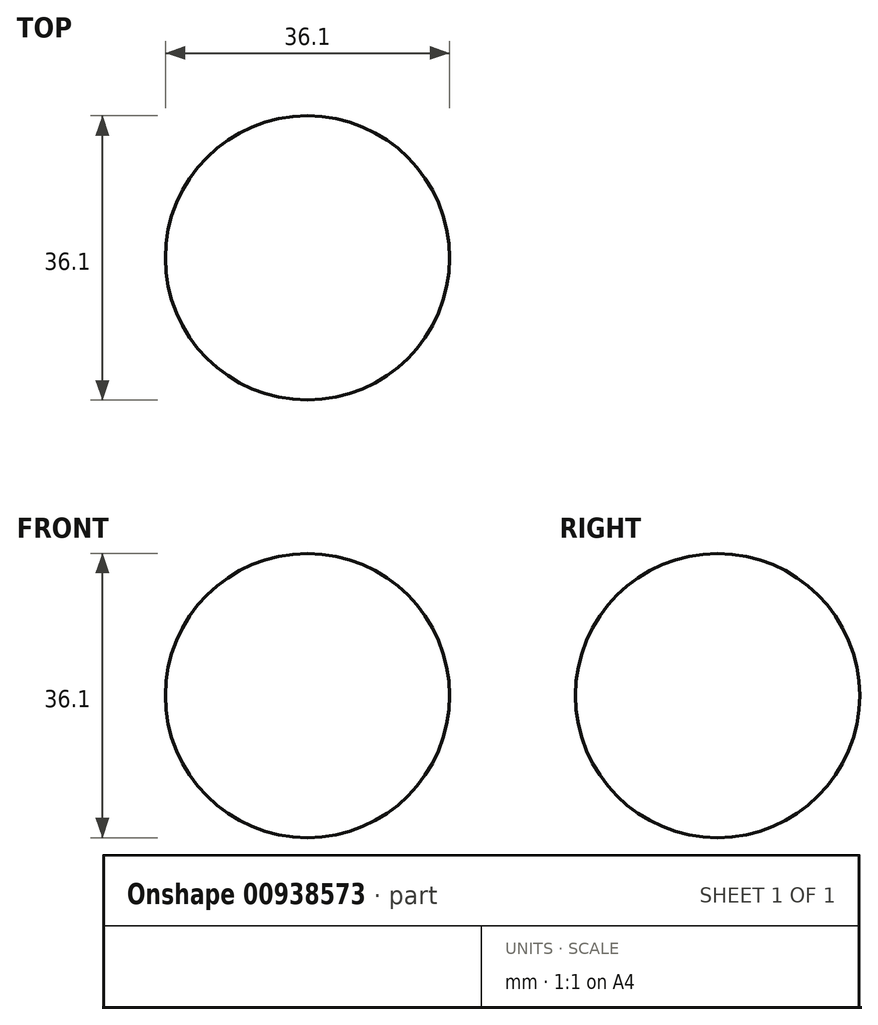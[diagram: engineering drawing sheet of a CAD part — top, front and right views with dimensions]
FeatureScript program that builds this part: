
annotation { "Feature Type Name" : "Feature", "Feature Type Description" : "" }
export const myFeature = defineFeature(function(context is Context, id is Id, definition is map)
    precondition{}
    {
        {
            var Q0;
            Q0=qCreatedBy(makeId("Top.planeOp"),FACE);
            var sketch = newSketch(context, id + "F0", { "sketchPlane" : qUnion([Q0])});
            skArc(sketch, "E0", {"start": v(18.05, 0) * mm, "mid": v(0, 18.05) * mm, "end": v(-18.05, 0) * mm});
            skLineSegment(sketch, "E1", {"start": v(-18.05, 0) * mm, "end": v(18.05, 0) * mm});
            skSolve(sketch);
        }
        {
            var Q0;
            Q0=makeQuery(id+"F0.imprint","IMPRINT",FACE,{"disambiguationData":[TD([[makeQuery(id+"F0.imprint","IMPRINT",EDGE,{"derivedFrom":sQuery(id+"F0.wireOp",EDGE,"E0")}),1.0]])]});
            var Q1;
            Q1=sQuery(id+"F0.wireOp",EDGE,"E1");
            revolve(context, id + "F1", {"surfaceOperationType" : NewSurfaceOperationType.NEW, "entities" : qUnion([Q0]), "axis" : qUnion([Q1]), "revolveType" : RevolveType.FULL});
        }
    });
